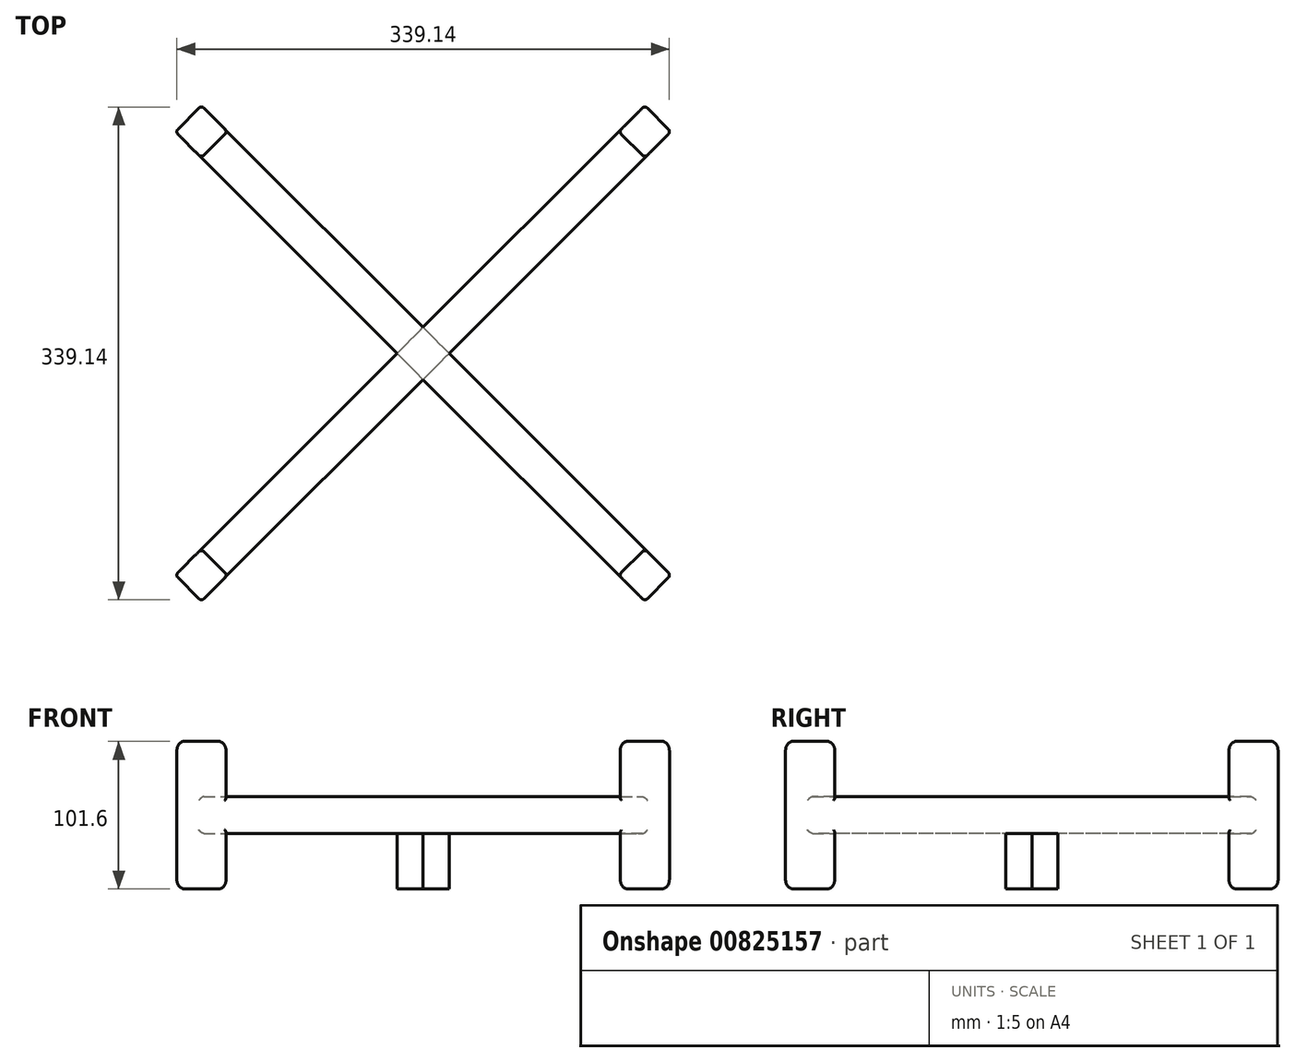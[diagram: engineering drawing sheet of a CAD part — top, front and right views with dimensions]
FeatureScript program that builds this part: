
annotation { "Feature Type Name" : "Feature", "Feature Type Description" : "" }
export const myFeature = defineFeature(function(context is Context, id is Id, definition is map)
    precondition{}
    {
        {
            var Q0;
            Q0=qCreatedBy(makeId("Front.planeOp"),FACE);
            var sketch = newSketch(context, id + "F0", { "sketchPlane" : qUnion([Q0])});
            skLineSegment(sketch, "E0", {"start": v(0, 75.69) * mm, "end": v(0, -77.72) * mm, "construction": true});
            skSolve(sketch);
        }
        {
            var Q0;
            Q0=sQuery(id+"F0.wireOp",EDGE,"E0");
            cPlane(context, id + "F1", {"entities" : qUnion([Q0]), "cplaneType" : CPlaneType.LINE_ANGLE, "offset" : 25.4 * mm, "angle" : 45 * degree, "width" : 152.4 * mm, "height" : 152.4 * mm});
        }
        {
            var Q0;
            Q0=qCreatedBy(id+"F1.planeOp",FACE);
            var sketch = newSketch(context, id + "F2", { "sketchPlane" : qUnion([Q0])});
            skLineSegment(sketch, "E1.bottom", {"start": v(-228.6, 50.8) * mm, "end": v(-203.2, 50.8) * mm});
            skLineSegment(sketch, "E1.top", {"start": v(-228.6, -50.8) * mm, "end": v(-203.2, -50.8) * mm});
            skLineSegment(sketch, "E1.left", {"start": v(-228.6, 50.8) * mm, "end": v(-228.6, -50.8) * mm});
            skLineSegment(sketch, "E1.right", {"start": v(228.6, 50.8) * mm, "end": v(228.6, -50.8) * mm});
            skPoint(sketch, "E2", {"position": v(0, 0) * mm});
            skPoint(sketch, "E2.positionSnap0", {"position": v(0, 50.8) * mm});
            skPoint(sketch, "E3", {"position": v(228.6, 0) * mm});
            skLineSegment(sketch, "E4.bottom", {"start": v(-203.2, 12.7) * mm, "end": v(203.2, 12.7) * mm});
            skLineSegment(sketch, "E4.left", {"start": v(-203.2, 12.7) * mm, "end": v(-203.2, 50.8) * mm});
            skLineSegment(sketch, "E4.right", {"start": v(203.2, 12.7) * mm, "end": v(203.2, 50.8) * mm});
            skLineSegment(sketch, "E5.bottom", {"start": v(-203.2, -12.7) * mm, "end": v(203.2, -12.7) * mm});
            skLineSegment(sketch, "E5.left", {"start": v(-203.2, -12.7) * mm, "end": v(-203.2, -50.8) * mm});
            skLineSegment(sketch, "E5.right", {"start": v(203.2, -12.7) * mm, "end": v(203.2, -50.8) * mm});
            skLineSegment(sketch, "E6.trimOffspring", {"start": v(203.2, 50.8) * mm, "end": v(228.6, 50.8) * mm});
            skLineSegment(sketch, "E7.trimOffspring", {"start": v(203.2, -50.8) * mm, "end": v(228.6, -50.8) * mm});
            skPoint(sketch, "E8.orphan", {"position": v(203.2, -74.5) * mm});
            skSolve(sketch);
        }
        {
            var Q0;
            Q0=makeQuery(id+"F2.imprint","IMPRINT",FACE,{"disambiguationData":[TD([[makeQuery(id+"F2.imprint","IMPRINT",EDGE,{"derivedFrom":sQuery(id+"F2.wireOp",EDGE,"E1.bottom")}),-1.0]])]});
            extrude(context, id + "F3", {"entities" : qUnion([Q0]), "depth" : 12.7 * mm, "offsetDistance" : 25.4 * mm, "hasSecondDirection" : true, "secondDirectionOppositeDirection" : true, "secondDirectionDepth" : 12.7 * mm});
        }
        {
            var Q0;
            Q0=makeQuery(id+"F3.opExtrude","SWEPT_EDGE",EDGE,{"disambiguationData":[OSD([sQuery(id+"F2.wireOp",EDGE,"E1.bottom"),sQuery(id+"F2.wireOp",EDGE,"E4.left")])]});
            var Q1;
            Q1=makeQuery(id+"F3.opExtrude","SWEPT_EDGE",EDGE,{"disambiguationData":[OSD([sQuery(id+"F2.wireOp",EDGE,"E4.right"),sQuery(id+"F2.wireOp",EDGE,"E6.trimOffspring")])]});
            var Q2;
            Q2=makeQuery(id+"F3.opExtrude","SWEPT_EDGE",EDGE,{"disambiguationData":[OSD([sQuery(id+"F2.wireOp",EDGE,"E1.top"),sQuery(id+"F2.wireOp",EDGE,"E1.left")])]});
            var Q3;
            Q3=makeQuery(id+"F3.opExtrude","SWEPT_EDGE",EDGE,{"disambiguationData":[OSD([sQuery(id+"F2.wireOp",EDGE,"E1.right"),sQuery(id+"F2.wireOp",EDGE,"E7.trimOffspring")])]});
            var Q4;
            Q4=makeQuery(id+"F3.opExtrude","SWEPT_EDGE",EDGE,{"disambiguationData":[OSD([sQuery(id+"F2.wireOp",EDGE,"E1.right"),sQuery(id+"F2.wireOp",EDGE,"E6.trimOffspring")])]});
            var Q5;
            Q5=makeQuery(id+"F3.opExtrude","SWEPT_EDGE",EDGE,{"disambiguationData":[OSD([sQuery(id+"F2.wireOp",EDGE,"E1.top"),sQuery(id+"F2.wireOp",EDGE,"E5.left")])]});
            var Q6;
            Q6=makeQuery(id+"F3.opExtrude","SWEPT_EDGE",EDGE,{"disambiguationData":[OSD([sQuery(id+"F2.wireOp",EDGE,"E1.bottom"),sQuery(id+"F2.wireOp",EDGE,"E1.left")])]});
            var Q7;
            Q7=makeQuery(id+"F3.opExtrude","SWEPT_EDGE",EDGE,{"disambiguationData":[OSD([sQuery(id+"F2.wireOp",EDGE,"E5.right"),sQuery(id+"F2.wireOp",EDGE,"E7.trimOffspring")])]});
            fillet(context, id + "F4", {"entities" : qUnion([Q0, Q1, Q2, Q3, Q4, Q5, Q6, Q7]), "radius" : 6.35 * mm, "tangentPropagation" : true, "allowEdgeOverflow" : false});
        }
        {
            var Q0;
            Q0=makeQuery(id+"F3.opExtrude","CAP_EDGE",EDGE,{"disambiguationData":[OSD([sQuery(id+"F2.wireOp",EDGE,"E1.left")])],"isStart":false});
            var Q1;
            Q1=makeQuery(id+"F3.opExtrude","CAP_EDGE",EDGE,{"disambiguationData":[OSD([sQuery(id+"F2.wireOp",EDGE,"E1.right")])],"isStart":false});
            var Q2;
            Q2=makeQuery(id+"F3.opExtrude","CAP_EDGE",EDGE,{"disambiguationData":[OSD([sQuery(id+"F2.wireOp",EDGE,"E1.right")])],"isStart":true});
            var Q3;
            Q3=makeQuery(id+"F3.opExtrude","CAP_EDGE",EDGE,{"disambiguationData":[OSD([sQuery(id+"F2.wireOp",EDGE,"E4.bottom")])],"isStart":false});
            var Q4;
            Q4=makeQuery(id+"F3.opExtrude","CAP_EDGE",EDGE,{"disambiguationData":[OSD([sQuery(id+"F2.wireOp",EDGE,"E4.bottom")])],"isStart":true});
            var Q5;
            Q5=makeQuery(id+"F3.opExtrude","CAP_EDGE",EDGE,{"disambiguationData":[OSD([sQuery(id+"F2.wireOp",EDGE,"E4.right")])],"isStart":false});
            var Q6;
            Q6=makeQuery(id+"F3.opExtrude","CAP_EDGE",EDGE,{"disambiguationData":[OSD([sQuery(id+"F2.wireOp",EDGE,"E5.bottom")])],"isStart":false});
            var Q7;
            Q7=makeQuery(id+"F3.opExtrude","CAP_EDGE",EDGE,{"disambiguationData":[OSD([sQuery(id+"F2.wireOp",EDGE,"E5.right")])],"isStart":false});
            var Q8;
            Q8=makeQuery(id+"F3.opExtrude","CAP_EDGE",EDGE,{"disambiguationData":[OSD([sQuery(id+"F2.wireOp",EDGE,"E5.left")])],"isStart":false});
            var Q9;
            Q9=makeQuery(id+"F3.opExtrude","CAP_EDGE",EDGE,{"disambiguationData":[OSD([sQuery(id+"F2.wireOp",EDGE,"E4.left")])],"isStart":false});
            var Q10;
            Q10=makeQuery(id+"F3.opExtrude","CAP_EDGE",EDGE,{"disambiguationData":[OSD([sQuery(id+"F2.wireOp",EDGE,"E4.left")])],"isStart":true});
            var Q11;
            Q11=makeQuery(id+"F3.opExtrude","SWEPT_EDGE",EDGE,{"disambiguationData":[OSD([sQuery(id+"F2.wireOp",EDGE,"E1.bottom"),sQuery(id+"F2.wireOp",EDGE,"E1.left")])]});
            var Q12;
            Q12=makeQuery(id+"F3.opExtrude","SWEPT_EDGE",EDGE,{"disambiguationData":[OSD([sQuery(id+"F2.wireOp",EDGE,"E1.right"),sQuery(id+"F2.wireOp",EDGE,"E6.trimOffspring")])]});
            var Q13;
            Q13=makeQuery(id+"F3.opExtrude","CAP_EDGE",EDGE,{"disambiguationData":[OSD([sQuery(id+"F2.wireOp",EDGE,"E5.right")])],"isStart":true});
            var Q14;
            Q14=makeQuery(id+"F3.opExtrude","CAP_EDGE",EDGE,{"disambiguationData":[OSD([sQuery(id+"F2.wireOp",EDGE,"E5.bottom")])],"isStart":true});
            var Q15;
            Q15=makeQuery(id+"F3.opExtrude","CAP_EDGE",EDGE,{"disambiguationData":[OSD([sQuery(id+"F2.wireOp",EDGE,"E4.right")])],"isStart":true});
            var Q16;
            {var subQ0=sQuery(id+"F2.wireOp",EDGE,"E6.trimOffspring");var subQ1=sQuery(id+"F2.wireOp",EDGE,"E4.right");Q16=makeQuery(id+"F4.opFillet","BLEND_EDGE",EDGE,{"blendedFrom":[makeQuery(id+"F3.opExtrude","SWEPT_EDGE",EDGE,{"disambiguationData":[OSD([subQ1,subQ0])]}),makeQuery(id+"F3.opExtrude","CAP_FACE",FACE,{"disambiguationData":[OSD([sQuery(id+"F2.wireOp",EDGE,"E1.bottom"),sQuery(id+"F2.wireOp",EDGE,"E1.top"),sQuery(id+"F2.wireOp",EDGE,"E1.left"),sQuery(id+"F2.wireOp",EDGE,"E1.right"),sQuery(id+"F2.wireOp",EDGE,"E4.bottom"),sQuery(id+"F2.wireOp",EDGE,"E4.left"),subQ1,sQuery(id+"F2.wireOp",EDGE,"E5.bottom"),sQuery(id+"F2.wireOp",EDGE,"E5.left"),sQuery(id+"F2.wireOp",EDGE,"E5.right"),subQ0,sQuery(id+"F2.wireOp",EDGE,"E7.trimOffspring")])],"isStart":true})],"blendedInto":[makeQuery(id+"F3.opExtrude","CAP_FACE",FACE,{"disambiguationData":[OSD([sQuery(id+"F2.wireOp",EDGE,"E1.bottom"),sQuery(id+"F2.wireOp",EDGE,"E1.top"),sQuery(id+"F2.wireOp",EDGE,"E1.left"),sQuery(id+"F2.wireOp",EDGE,"E1.right"),sQuery(id+"F2.wireOp",EDGE,"E4.bottom"),sQuery(id+"F2.wireOp",EDGE,"E4.left"),subQ1,sQuery(id+"F2.wireOp",EDGE,"E5.bottom"),sQuery(id+"F2.wireOp",EDGE,"E5.left"),sQuery(id+"F2.wireOp",EDGE,"E5.right"),subQ0,sQuery(id+"F2.wireOp",EDGE,"E7.trimOffspring")])],"isStart":true})]});}
            var Q17;
            Q17=makeQuery(id+"F3.opExtrude","SWEPT_EDGE",EDGE,{"disambiguationData":[OSD([sQuery(id+"F2.wireOp",EDGE,"E5.right"),sQuery(id+"F2.wireOp",EDGE,"E7.trimOffspring")])]});
            var Q18;
            Q18=makeQuery(id+"F3.opExtrude","CAP_EDGE",EDGE,{"disambiguationData":[OSD([sQuery(id+"F2.wireOp",EDGE,"E5.left")])],"isStart":true});
            var Q19;
            Q19=makeQuery(id+"F3.opExtrude","CAP_EDGE",EDGE,{"disambiguationData":[OSD([sQuery(id+"F2.wireOp",EDGE,"E1.top")])],"isStart":true});
            fillet(context, id + "F5", {"entities" : qUnion([Q0, Q1, Q2, Q3, Q4, Q5, Q6, Q7, Q8, Q9, Q10, Q11, Q12, Q13, Q14, Q15, Q16, Q17, Q18, Q19]), "radius" : 2.54 * mm, "tangentPropagation" : true, "allowEdgeOverflow" : false});
        }
        {
            var Q0;
            Q0=qCreatedBy(makeId("Front.planeOp"),FACE);
            var sketch = newSketch(context, id + "F6", { "sketchPlane" : qUnion([Q0])});
            skLineSegment(sketch, "E9", {"start": v(0, -74.1) * mm, "end": v(0, 72) * mm, "construction": true});
            skSolve(sketch);
        }
        {
            var Q0;
            Q0=makeQuery(id+"F3.opExtrude","SWEPT_BODY",BODY,{"disambiguationData":[OSD([sQuery(id+"F2.wireOp",EDGE,"E1.bottom"),sQuery(id+"F2.wireOp",EDGE,"E1.top"),sQuery(id+"F2.wireOp",EDGE,"E1.left"),sQuery(id+"F2.wireOp",EDGE,"E1.right"),sQuery(id+"F2.wireOp",EDGE,"E4.bottom"),sQuery(id+"F2.wireOp",EDGE,"E4.left"),sQuery(id+"F2.wireOp",EDGE,"E4.right"),sQuery(id+"F2.wireOp",EDGE,"E5.bottom"),sQuery(id+"F2.wireOp",EDGE,"E5.left"),sQuery(id+"F2.wireOp",EDGE,"E5.right"),sQuery(id+"F2.wireOp",EDGE,"E6.trimOffspring"),sQuery(id+"F2.wireOp",EDGE,"E7.trimOffspring")])]});
            var Q1;
            Q1=sQuery(id+"F6.wireOp",EDGE,"E9");
            circularPattern(context, id + "F7", {"entities" : qUnion([Q0]), "axis" : qUnion([Q1]), "angle" : 90 * degree, "instanceCount" : 2, "equalSpace" : true});
        }
        {
            var Q0;
            Q0=makeQuery(id+"F3.opExtrude","SWEPT_FACE",FACE,{"disambiguationData":[OSD([sQuery(id+"F2.wireOp",EDGE,"E5.bottom")])]});
            var sketch = newSketch(context, id + "F8", { "sketchPlane" : qUnion([Q0])});
            skLineSegment(sketch, "E10.bottom", {"start": v(0, 17.96) * mm, "end": v(-17.96, 0) * mm});
            skLineSegment(sketch, "E10.top", {"start": v(17.96, 0) * mm, "end": v(0, -17.96) * mm});
            skLineSegment(sketch, "E10.left", {"start": v(0, 17.96) * mm, "end": v(17.96, 0) * mm});
            skLineSegment(sketch, "E10.right", {"start": v(-17.96, 0) * mm, "end": v(0, -17.96) * mm});
            skPoint(sketch, "E10.middle", {"position": v(0, 0) * mm});
            skSolve(sketch);
        }
        {
            var Q0;
            Q0 = qSketchRegion(id + "F8", true);
            extrude(context, id + "F9", {"entities" : qUnion([Q0]), "depth" : 38.1 * mm, "offsetDistance" : 25.4 * mm});
        }
    });
